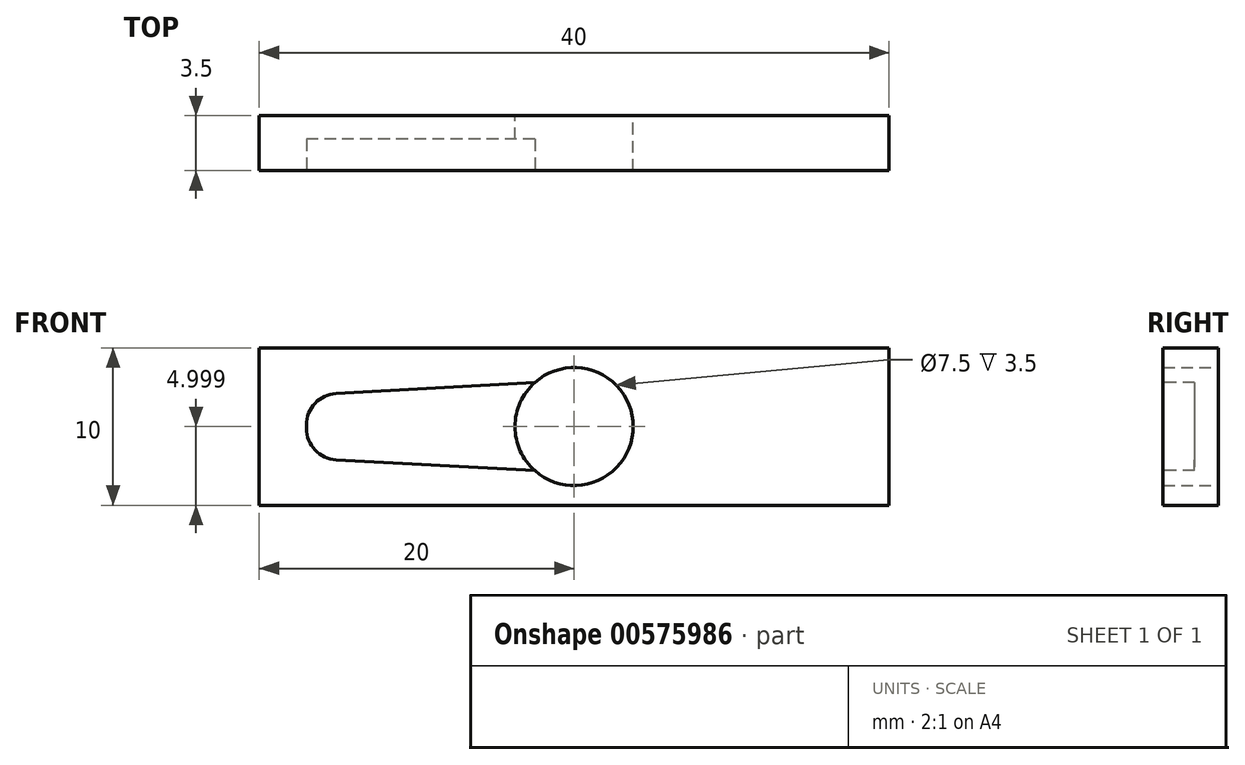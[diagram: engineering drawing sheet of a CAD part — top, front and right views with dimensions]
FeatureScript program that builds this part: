
annotation { "Feature Type Name" : "Feature", "Feature Type Description" : "" }
export const myFeature = defineFeature(function(context is Context, id is Id, definition is map)
    precondition{}
    {
        {
            var Q0;
            Q0=qCreatedBy(makeId("Front.planeOp"),FACE);
            var sketch = newSketch(context, id + "F0", { "sketchPlane" : qUnion([Q0])});
            skLineSegment(sketch, "E0.bottom", {"start": v(0, 2.3) * mm, "end": v(40, 2.3) * mm});
            skLineSegment(sketch, "E0.top", {"start": v(0, 12.3) * mm, "end": v(40, 12.3) * mm});
            skLineSegment(sketch, "E0.left", {"start": v(0, 2.3) * mm, "end": v(0, 12.3) * mm});
            skLineSegment(sketch, "E0.right", {"start": v(40, 2.3) * mm, "end": v(40, 12.3) * mm});
            skPoint(sketch, "E1", {"position": v(20, 12.3) * mm});
            skPoint(sketch, "E2", {"position": v(40, 7.3) * mm});
            skCircle(sketch, "E3", {"center": v(20, 7.3) * mm, "radius": 3.75 * mm});
            skSolve(sketch);
        }
        {
            var Q0;
            Q0=makeQuery(id+"F0.imprint","IMPRINT",FACE,{"disambiguationData":[TD([[makeQuery(id+"F0.imprint","IMPRINT",EDGE,{"derivedFrom":sQuery(id+"F0.wireOp",EDGE,"E0.bottom")}),1.0]])]});
            extrude(context, id + "F1", {"entities" : qUnion([Q0]), "depth" : 3.5 * mm, "offsetDistance" : 25 * mm});
        }
        {
            var Q0;
            Q0=makeQuery(id+"F1.opExtrude","CAP_FACE",FACE,{"disambiguationData":[OSD([sQuery(id+"F0.wireOp",EDGE,"E0.bottom"),sQuery(id+"F0.wireOp",EDGE,"E0.top"),sQuery(id+"F0.wireOp",EDGE,"E0.left"),sQuery(id+"F0.wireOp",EDGE,"E0.right"),sQuery(id+"F0.wireOp",EDGE,"E3")])],"isStart":false});
            var sketch = newSketch(context, id + "F2", { "sketchPlane" : qUnion([Q0])});
            skLineSegment(sketch, "E4.left", {"start": v(17.5, 10.1) * mm, "end": v(17.5, 4.5) * mm});
            skLineSegment(sketch, "E4.right", {"start": v(3, 7.4) * mm, "end": v(3, 7.2) * mm});
            skCircle(sketch, "E5.0", {"center": v(20, 7.3) * mm, "radius": 3.75 * mm, "construction": true});
            skLineSegment(sketch, "E6", {"start": v(17.5, 10.1) * mm, "end": v(4.89, 9.4) * mm});
            skLineSegment(sketch, "E7", {"start": v(17.5, 4.5) * mm, "end": v(4.89, 5.2) * mm});
            skLineSegment(sketch, "E8", {"start": v(3, 9.3) * mm, "end": v(3, 10.1) * mm, "construction": true});
            skLineSegment(sketch, "E9", {"start": v(3, 5.3) * mm, "end": v(3, 4.5) * mm, "construction": true});
            skArc(sketch, "E10.filletArc", {"start": v(4.89, 9.4) * mm, "mid": v(3.55, 8.78) * mm, "end": v(3, 7.4) * mm});
            skArc(sketch, "E11.filletArc", {"start": v(3, 7.2) * mm, "mid": v(3.55, 5.82) * mm, "end": v(4.89, 5.2) * mm});
            skSolve(sketch);
        }
        {
            var Q0;
            Q0=makeQuery(id+"F2.imprint","IMPRINT",FACE,{"disambiguationData":[TD([[makeQuery(id+"F2.imprint","IMPRINT",EDGE,{"derivedFrom":sQuery(id+"F2.wireOp",EDGE,"E4.right")}),1.0]])]});
            extrude(context, id + "F3", {"entities" : qUnion([Q0]), "operationType" : NewBodyOperationType.REMOVE, "oppositeDirection" : true, "depth" : 2 * mm, "offsetDistance" : 25 * mm});
        }
        {
            var Q0;
            Q0=makeQuery(id+"F1.opExtrude","CAP_EDGE",EDGE,{"disambiguationData":[OSD([sQuery(id+"F0.wireOp",EDGE,"E0.bottom")])],"isStart":false});
            cPoint(context, id + "F4", {"entities" : qUnion([Q0]), "parameter" : 0.5});
        }
        {
            var Q0;
            Q0=makeQuery(id+"F1.opExtrude","CAP_EDGE",EDGE,{"disambiguationData":[OSD([sQuery(id+"F0.wireOp",EDGE,"E3")])],"isStart":false});
            var Q1;
            Q1 = qCreatedBy(id + "F4" ,VERTEX);
            cPlane(context, id + "F5", {"entities" : qUnion([Q0, Q1]), "cplaneType" : CPlaneType.CURVE_POINT, "offset" : 25 * mm, "width" : 150 * mm, "height" : 150 * mm});
        }
    });
